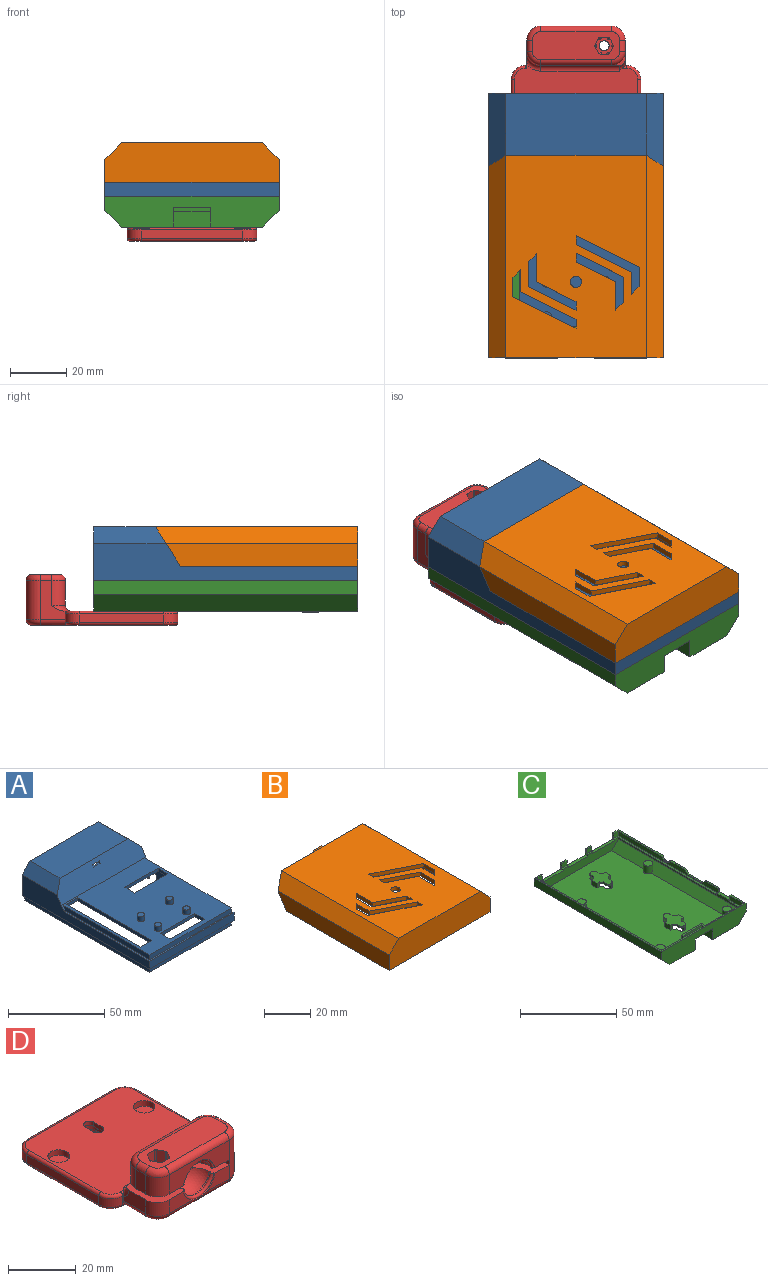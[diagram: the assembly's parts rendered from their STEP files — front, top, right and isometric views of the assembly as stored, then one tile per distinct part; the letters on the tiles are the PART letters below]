
ASSEMBLY  parts=4 mates=1
PART A: 83 faces, bbox 62x94x22 mm
  f0: plane 94x62mm, normal (0,0,-1), area 195.6mm2, adj f3,f4,f11,f16,f26,f27,f28,f43
  f1: plane 64x3mm, normal (-1,0,0), area 189.1mm2, adj f2,f25,f37,f39
  f2: plane 64x60mm, normal (0,0,1), area 2976.4mm2, adj f1,f25,f38,f39,f63,f64,f65,f66
  f3: plane 94x13mm, normal (-1,0,0), area 696.9mm2, adj f0,f4,f24,f25,f26,f37
  f4: plane 62x5mm, normal (0,-1,0), area 310mm2, adj f0,f3,f27,f37
  f5: plane 14.2x2mm, normal (0,0,-1), area 28.4mm2, adj f16,f17,f26,f29
  f6: plane 14.2x2mm, normal (0,0,-1), area 28.4mm2, adj f18,f19,f26,f29
  f7: plane 16.2x2mm, normal (0,0,-1), area 32.4mm2, adj f20,f21,f26,f29
  f8: plane 15.4x2mm, normal (0,0,-1), area 30.8mm2, adj f10,f11,f27,f28
  f9: cylinder r=3.1mm len=6.2mm, axis (1,0,0), area 23.1mm2, adj f14,f15,f27,f28,f54,f57
  f10: plane 7.2x2mm, normal (0,-1,0), area 11.4mm2, adj f8,f14,f27,f28,f58,f59
  f11: plane 7.2x2mm, normal (0,1,0), area 11.4mm2, adj f0,f8,f27,f28,f60,f62
  f12: plane 3.8x1mm, normal (0,0,-1), area 3.8mm2, adj f19,f20,f26,f51
  f13: plane 4x1mm, normal (0,0,-1), area 4mm2, adj f17,f18,f26,f49
  f14: plane 10.63x1mm, normal (0,0,-1), area 10.6mm2, adj f9,f10,f27,f58
  f15: plane 33.03x4.4mm, normal (0,0,-1), area 36.4mm2, adj f9,f21,f26,f27,f53,f55
  f16: plane 14.05x2mm, normal (1,0,0), area 25.1mm2, adj f0,f5,f26,f29,f44,f48
  f17: plane 14.05x2mm, normal (-1,0,0), area 25.1mm2, adj f5,f13,f26,f29,f49,f50
  f18: plane 14.05x2mm, normal (1,0,0), area 25.1mm2, adj f6,f13,f26,f29,f49,f50
  f19: plane 14.05x2mm, normal (-1,0,0), area 25.1mm2, adj f6,f12,f26,f29,f51,f52
  f20: plane 13.05x2mm, normal (1,0,0), area 23.1mm2, adj f7,f12,f26,f29,f51,f52
  f21: plane 13.05x2mm, normal (-1,0,0), area 23.1mm2, adj f7,f15,f26,f29,f55,f56
  f22: plane 25.82x6mm, normal (0.71,0,0.71), area 202.9mm2, adj f23,f25,f26,f27
  f23: plane 50x22mm, normal (0,0,1), area 1100mm2, adj f22,f24,f25,f26
  f24: plane 25.82x6mm, normal (-0.71,0,0.71), area 202.9mm2, adj f3,f23,f25,f26
  f25: plane 62x14mm, normal (0,-0.84,0.54), area 765.6mm2, adj f1,f2,f3,f22,f23,f24,f27,f33
  f26: plane 62x19mm, normal (0,1,0), area 665.4mm2, adj f0,f3,f5,f6,f7,f12,f13,f15
  f27: plane 94x13mm, normal (1,0,0), area 611.6mm2, adj f0,f4,f8,f9,f10,f11,f14,f15
  f28: plane 90x16mm, normal (-1,0,0), area 808.9mm2, adj f0,f8,f9,f10,f11,f29,f30,f31
  f29: plane 58x20mm, normal (0,-1,0), area 533.6mm2, adj f5,f6,f7,f16,f17,f18,f19,f20
  f30: plane 63x58mm, normal (0,0,-1), area 2835.8mm2, adj f28,f31,f35,f36,f63,f64,f65,f66
  f31: plane 58x11mm, normal (0,0.84,-0.54), area 730mm2, adj f28,f30,f32,f33,f34,f36,f40,f41
  f32: plane 22.55x4mm, normal (-0.71,0,-0.71), area 120.3mm2, adj f28,f29,f31,f33
  f33: plane 50x21.27mm, normal (0,0,-1), area 1006.5mm2, adj f25,f29,f31,f32,f34,f40,f41
  f34: plane 22.55x4mm, normal (0.71,0,-0.71), area 120.3mm2, adj f29,f31,f33,f36
  f35: plane 58x9mm, normal (0,1,0), area 522mm2, adj f28,f30,f36,f48
  f36: plane 90x16mm, normal (1,0,0), area 983.4mm2, adj f29,f30,f31,f34,f35,f48
  f37: plane 63.09x62mm, normal (0,0,1), area 186.2mm2, adj f1,f3,f4,f25,f27,f38,f39
  f38: plane 64x3mm, normal (1,0,0), area 189.1mm2, adj f2,f25,f37,f39
  f39: plane 60x3mm, normal (0,-1,0), area 180mm2, adj f1,f2,f37,f38
  f40: plane 2.04x1.2mm, normal (1,0,0), area 1.5mm2, adj f25,f31,f33,f42
  f41: plane 2.04x1.2mm, normal (-1,0,0), area 1.5mm2, adj f25,f31,f33,f42
  f42: plane 5.1x1.27mm, normal (0,0,1), area 6.5mm2, adj f25,f31,f40,f41
  f43: plane 92x3mm, normal (-1,0,0), area 276mm2, adj f0,f44,f47,f48
  f44: plane 4.2x3mm, normal (0,1,0), area 12.6mm2, adj f0,f16,f43,f48
  f45: plane 3x1mm, normal (0,1,0), area 3mm2, adj f0,f28,f46,f48
  f46: plane 10x3mm, normal (1,0,0), area 30mm2, adj f0,f45,f47,f48
  f47: plane 60x3mm, normal (0,-1,0), area 180mm2, adj f0,f43,f46,f48
  f48: plane 92x60mm, normal (0,0,-1), area 163.2mm2, adj f16,f28,f29,f35,f36,f43,f44,f45
  f49: plane 4x3mm, normal (0,1,0), area 12mm2, adj f13,f17,f18,f50
  f50: plane 4x1mm, normal (0,0,-1), area 4mm2, adj f17,f18,f29,f49
  f51: plane 3.8x3mm, normal (0,1,0), area 11.4mm2, adj f12,f19,f20,f52
  f52: plane 3.8x1mm, normal (0,0,-1), area 3.8mm2, adj f19,f20,f29,f51
  f53: plane 32.03x3mm, normal (1,0,0), area 96.1mm2, adj f15,f54,f55,f56
  f54: plane 3x1mm, normal (0,-1,0), area 3mm2, adj f9,f28,f53,f56
  f55: plane 3.4x3mm, normal (0,1,0), area 10.2mm2, adj f15,f21,f53,f56
  f56: plane 32.03x3.4mm, normal (0,0,-1), area 34.4mm2, adj f21,f28,f29,f53,f54,f55
  f57: plane 3x1mm, normal (0,1,0), area 3mm2, adj f9,f28,f58,f59
  f58: plane 10.63x3mm, normal (1,0,0), area 31.9mm2, adj f10,f14,f57,f59
  f59: plane 10.63x1mm, normal (0,0,-1), area 10.6mm2, adj f10,f28,f57,f58
  f60: plane 9.6x3mm, normal (1,0,0), area 28.8mm2, adj f0,f11,f61,f62
  f61: plane 3x1mm, normal (0,-1,0), area 3mm2, adj f0,f28,f60,f62
  f62: plane 9.6x1mm, normal (0,0,-1), area 9.6mm2, adj f11,f28,f60,f61
  f63: plane 7.3x2mm, normal (1,0,0), area 14.6mm2, adj f2,f30,f64,f65
  f64: plane 24.4x2mm, normal (0,-1,0), area 48.8mm2, adj f2,f30,f63,f66
  f65: plane 24.4x2mm, normal (0,1,0), area 48.8mm2, adj f2,f30,f63,f66
  f66: plane 7.3x2mm, normal (-1,0,0), area 14.6mm2, adj f2,f30,f64,f65
  f67: plane 7.2x2mm, normal (1,0,0), area 14.4mm2, adj f2,f30,f68,f69
  f68: plane 25.2x2mm, normal (0,-1,0), area 50.4mm2, adj f2,f30,f67,f70
  f69: plane 25.2x2mm, normal (0,1,0), area 50.4mm2, adj f2,f30,f67,f70
  f70: plane 7.2x2mm, normal (-1,0,0), area 14.4mm2, adj f2,f30,f68,f69
  f71: plane 54.6x2mm, normal (1,0,0), area 109.2mm2, adj f2,f30,f72,f73
  f72: plane 8.4x2mm, normal (0,-1,0), area 16.8mm2, adj f2,f30,f71,f74
  f73: plane 8.4x2mm, normal (0,1,0), area 16.8mm2, adj f2,f30,f71,f74
  f74: plane 54.6x2mm, normal (-1,0,0), area 109.2mm2, adj f2,f30,f72,f73
  f75: cylinder r=1.9mm len=3.8mm, axis (0,0,-1), area 35.8mm2, adj f2,f76
  f76: plane 3.8x3.8mm, normal (0,0,1), area 11.3mm2, adj f75
  f77: cylinder r=1.9mm len=3.8mm, axis (0,0,-1), area 35.8mm2, adj f2,f78
  f78: plane 3.8x3.8mm, normal (0,0,1), area 11.3mm2, adj f77
  f79: cylinder r=1.9mm len=3.8mm, axis (0,0,-1), area 35.8mm2, adj f2,f80
  f80: plane 3.8x3.8mm, normal (0,0,1), area 11.3mm2, adj f79
  f81: cylinder r=1.9mm len=3.8mm, axis (0,0,-1), area 35.8mm2, adj f2,f82
  f82: plane 3.8x3.8mm, normal (0,0,1), area 11.3mm2, adj f81
PART B: 55 faces, bbox 62x74.9x14 mm
  f0: plane 68.18x8mm, normal (1,0,0), area 525.1mm2, adj f4,f6,f7,f54
  f1: plane 68.18x8mm, normal (-1,0,0), area 525.1mm2, adj f4,f6,f8,f54
  f2: plane 68.73x4.83mm, normal (-0.71,0,-0.71), area 446.1mm2, adj f4,f35,f36,f37,f42,f43,f44
  f3: plane 68.73x4.83mm, normal (0.71,0,-0.71), area 446.1mm2, adj f4,f35,f36,f38,f39,f40,f41
  f4: plane 62x14mm, normal (0,0.84,-0.54), area 181.7mm2, adj f0,f1,f2,f3,f5,f7,f8,f9
  f5: plane 72x50mm, normal (0,0,1), area 3265.5mm2, adj f4,f6,f7,f8,f10,f11,f12,f13
  f6: plane 62x14mm, normal (0,-1,0), area 832mm2, adj f0,f1,f5,f7,f8,f54
  f7: plane 72x6mm, normal (0.71,0,0.71), area 594.7mm2, adj f0,f4,f5,f6
  f8: plane 72x6mm, normal (-0.71,0,0.71), area 594.7mm2, adj f1,f4,f5,f6
  f9: plane 64x60mm, normal (0,0,-1), area 186mm2, adj f4,f36,f37,f38,f51,f52,f53
  f10: cylinder r=2mm len=4mm, axis (0,0,1), area 25.1mm2, adj f5,f35
  f11: plane 3.13x2mm, normal (-1,0,0), area 6.3mm2, adj f5,f12,f16,f35
  f12: plane 19.6x9.8mm, normal (-0.45,-0.89,0), area 43.8mm2, adj f5,f11,f13,f35
  f13: plane 7.86x2mm, normal (-1,0,0), area 15.7mm2, adj f5,f12,f14,f35
  f14: plane 2.8x2.8mm, normal (0.71,-0.71,0), area 7.9mm2, adj f5,f13,f15,f35
  f15: plane 6.79x2mm, normal (1,0,0), area 13.6mm2, adj f5,f14,f16,f35
  f16: plane 22.4x11.2mm, normal (0.45,0.89,0), area 50.1mm2, adj f5,f11,f15,f35
  f17: plane 3.13x2mm, normal (1,0,0), area 6.3mm2, adj f5,f18,f22,f35
  f18: plane 14x7mm, normal (0.45,0.89,0), area 31.3mm2, adj f5,f17,f19,f35
  f19: plane 10x2mm, normal (1,0,0), area 20mm2, adj f5,f18,f20,f35
  f20: plane 2.8x2.8mm, normal (-0.71,0.71,0), area 7.9mm2, adj f5,f19,f21,f35
  f21: plane 8.93x2mm, normal (-1,0,0), area 17.9mm2, adj f5,f20,f22,f35
  f22: plane 16.8x8.4mm, normal (-0.45,-0.89,0), area 37.6mm2, adj f5,f17,f21,f35
  f23: plane 3.13x2mm, normal (-1,0,0), area 6.3mm2, adj f5,f24,f28,f35
  f24: plane 14x7mm, normal (-0.45,-0.89,0), area 31.3mm2, adj f5,f23,f25,f35
  f25: plane 10x2mm, normal (-1,0,0), area 20mm2, adj f5,f24,f26,f35
  f26: plane 2.8x2.8mm, normal (0.71,-0.71,0), area 7.9mm2, adj f5,f25,f27,f35
  f27: plane 8.93x2mm, normal (1,0,0), area 17.9mm2, adj f5,f26,f28,f35
  f28: plane 16.8x8.4mm, normal (0.45,0.89,0), area 37.6mm2, adj f5,f23,f27,f35
  f29: plane 3.13x2mm, normal (1,0,0), area 6.3mm2, adj f5,f30,f34,f35
  f30: plane 19.6x9.8mm, normal (0.45,0.89,0), area 43.8mm2, adj f5,f29,f31,f35
  f31: plane 7.86x2mm, normal (1,0,0), area 15.7mm2, adj f5,f30,f32,f35
  f32: plane 2.8x2.8mm, normal (-0.71,0.71,0), area 7.9mm2, adj f5,f31,f33,f35
  f33: plane 6.79x2mm, normal (-1,0,0), area 13.6mm2, adj f5,f32,f34,f35
  f34: plane 22.4x11.2mm, normal (-0.45,-0.89,0), area 50.1mm2, adj f5,f29,f33,f35
  f35: plane 68.73x48.8mm, normal (0,0,-1), area 2984.5mm2, adj f2,f3,f4,f10,f11,f12,f13,f14
  f36: plane 58x9mm, normal (0,1,0), area 498.7mm2, adj f2,f3,f9,f35,f37,f38
  f37: plane 65.65x4.17mm, normal (-1,0,0), area 268.3mm2, adj f2,f4,f9,f36
  f38: plane 65.65x4.17mm, normal (1,0,0), area 268.3mm2, adj f3,f4,f9,f36
  f39: plane 0.23x0.23mm, normal (0,-1,0), area 0mm2, adj f3,f35,f40
  f40: plane 39.26x0.23mm, normal (1,0,0), area 9mm2, adj f3,f35,f39,f41
  f41: plane 0.23x0.23mm, normal (0,1,0), area 0mm2, adj f3,f35,f40
  f42: plane 39.26x0.23mm, normal (-1,0,0), area 9mm2, adj f2,f35,f43,f44
  f43: plane 0.23x0.23mm, normal (0,-1,0), area 0mm2, adj f2,f35,f42
  f44: plane 0.23x0.23mm, normal (0,1,0), area 0mm2, adj f2,f35,f42
  f45: plane 5.1x4.2mm, normal (0,0,1), area 21.4mm2, adj f4,f46,f47,f48
  f46: plane 8.4x1.2mm, normal (-1,0,0), area 10.1mm2, adj f35,f45,f47,f49,f50
  f47: plane 5.1x1.2mm, normal (0,1,0), area 6.1mm2, adj f45,f46,f48,f50
  f48: plane 8.4x1.2mm, normal (1,0,0), area 10.1mm2, adj f35,f45,f47,f49,f50
  f49: plane 5.1x1.2mm, normal (0,-1,0), area 6.1mm2, adj f35,f46,f48,f50
  f50: plane 8.4x5.1mm, normal (0,0,-1), area 42.8mm2, adj f46,f47,f48,f49
  f51: plane 64x3mm, normal (1,0,0), area 189.1mm2, adj f4,f9,f52,f54
  f52: plane 60x3mm, normal (0,1,0), area 180mm2, adj f9,f51,f53,f54
  f53: plane 64x3mm, normal (-1,0,0), area 189.1mm2, adj f4,f9,f52,f54
  f54: plane 63.09x62mm, normal (0,0,-1), area 186.2mm2, adj f0,f1,f4,f6,f51,f52,f53
PART C: 143 faces, bbox 62x94x11.6 mm
  f0: plane 90x48.34mm, normal (0,0,1), area 4043.5mm2, adj f1,f2,f4,f17,f55,f56,f57,f58
  f1: plane 90x4.83mm, normal (0.71,0,0.71), area 582.2mm2, adj f0,f4,f17,f71,f135,f141
  f2: plane 90x4.83mm, normal (-0.71,0,0.71), area 582.2mm2, adj f0,f4,f17,f18,f137,f139
  f3: plane 94x50mm, normal (0,0,-1), area 3255.1mm2, adj f25,f26,f33,f34,f36,f37,f38,f40
  f4: plane 58x6mm, normal (0,1,0), area 252.7mm2, adj f0,f1,f2,f18,f25,f26,f27,f71
  f5: plane 3.95x2mm, normal (-1,0,0), area 4.9mm2, adj f9,f17,f22,f34,f84,f85
  f6: plane 3.95x2mm, normal (-1,0,0), area 4.9mm2, adj f10,f17,f23,f34,f82,f83
  f7: plane 3.95x2mm, normal (-1,0,0), area 4.9mm2, adj f11,f17,f24,f34,f79,f80
  f8: plane 94x62mm, normal (0,0,1), area 169.2mm2, adj f14,f15,f32,f33,f34,f35,f73,f74
  f9: plane 4x1mm, normal (0,0,1), area 4mm2, adj f5,f19,f34,f84
  f10: plane 3.8x1mm, normal (0,0,1), area 3.8mm2, adj f6,f20,f34,f83
  f11: plane 33.03x4.4mm, normal (0,0,1), area 36.4mm2, adj f7,f21,f32,f34,f80,f81
  f12: plane 10.63x1mm, normal (0,0,1), area 10.6mm2, adj f21,f30,f32,f81
  f13: plane 9.6x1mm, normal (0,0,1), area 9.6mm2, adj f16,f28,f32,f81
  f14: plane 3.95x2mm, normal (1,0,0), area 4.9mm2, adj f8,f17,f22,f34,f72,f77
  f15: plane 2.2x1mm, normal (0,1,0), area 2.2mm2, adj f8,f31,f32,f76
  f16: plane 2.2x1mm, normal (0,-1,0), area 2.2mm2, adj f13,f31,f32,f81
  f17: plane 58x6mm, normal (0,-1,0), area 282.3mm2, adj f0,f1,f2,f5,f6,f7,f14,f18
  f18: plane 90x1.97mm, normal (-1,0,0), area 112.2mm2, adj f2,f4,f17,f31,f72,f75,f78,f79
  f19: plane 3.95x2mm, normal (1,0,0), area 4.9mm2, adj f9,f17,f23,f34,f84,f85
  f20: plane 3.95x2mm, normal (1,0,0), area 4.9mm2, adj f10,f17,f24,f34,f82,f83
  f21: cylinder r=3.1mm len=5.93mm, axis (1,0,0), area 7.9mm2, adj f11,f12,f32,f81
  f22: plane 14.2x2mm, normal (0,0,1), area 28.4mm2, adj f5,f14,f17,f34
  f23: plane 14.2x2mm, normal (0,0,1), area 28.4mm2, adj f6,f17,f19,f34
  f24: plane 16.2x2mm, normal (0,0,1), area 32.4mm2, adj f7,f17,f20,f34
  f25: plane 8x7mm, normal (-1,0,0), area 47mm2, adj f3,f4,f27,f33,f38,f129
  f26: plane 8x7mm, normal (1,0,0), area 47mm2, adj f3,f4,f27,f33,f38,f129
  f27: plane 13x2mm, normal (0,0,-1), area 26mm2, adj f4,f25,f26,f33
  f28: plane 2.7x2.2mm, normal (0,0.63,0.78), area 3.5mm2, adj f13,f29,f32,f81
  f29: plane 10x1mm, normal (0,0,1), area 10mm2, adj f28,f30,f32,f81
  f30: plane 2.7x2.2mm, normal (0,-0.63,0.78), area 3.5mm2, adj f12,f29,f32,f81
  f31: plane 8.4x2mm, normal (0,0,1), area 16.8mm2, adj f15,f16,f18,f32,f75,f78
  f32: plane 94x5mm, normal (1,0,0), area 414mm2, adj f8,f11,f12,f13,f15,f16,f21,f28
  f33: plane 62x11mm, normal (0,-1,0), area 555mm2, adj f3,f8,f25,f26,f27,f32,f35,f36
  f34: plane 62x11mm, normal (0,1,0), area 469.8mm2, adj f3,f5,f6,f7,f8,f9,f10,f11
  f35: plane 94x5mm, normal (-1,0,0), area 470mm2, adj f8,f33,f34,f36
  f36: plane 94x6mm, normal (-0.71,0,-0.71), area 797.6mm2, adj f3,f33,f34,f35
  f37: plane 94x6mm, normal (0.71,0,-0.71), area 797.6mm2, adj f3,f32,f33,f34
  f38: plane 13x5.5mm, normal (0,-1,0), area 71.5mm2, adj f3,f25,f26,f129
  f39: cylinder r=1.8mm len=3.6mm, axis (0,0,1), area 6.8mm2, adj f41,f42
  f40: cylinder r=2.85mm len=5.7mm, axis (0,0,1), area 10.7mm2, adj f3,f41
  f41: plane 5.7x5.7mm, normal (0,0,-1), area 15.3mm2, adj f39,f40
  f42: plane 3.6x3.6mm, normal (0,0,-1), area 10.2mm2, adj f39
  f43: cylinder r=1.8mm len=3.6mm, axis (0,0,1), area 6.8mm2, adj f45,f46
  f44: cylinder r=2.85mm len=5.7mm, axis (0,0,1), area 10.7mm2, adj f3,f45
  f45: plane 5.7x5.7mm, normal (0,0,-1), area 15.3mm2, adj f43,f44
  f46: plane 3.6x3.6mm, normal (0,0,-1), area 10.2mm2, adj f43
  f47: cylinder r=1.8mm len=3.6mm, axis (0,0,1), area 6.8mm2, adj f49,f50
  f48: cylinder r=2.85mm len=5.7mm, axis (0,0,1), area 10.7mm2, adj f3,f49
  f49: plane 5.7x5.7mm, normal (0,0,-1), area 15.3mm2, adj f47,f48
  f50: plane 3.6x3.6mm, normal (0,0,-1), area 10.2mm2, adj f47
  f51: cylinder r=1.8mm len=3.6mm, axis (0,0,1), area 6.8mm2, adj f53,f54
  f52: cylinder r=2.85mm len=5.7mm, axis (0,0,1), area 10.7mm2, adj f3,f53
  f53: plane 5.7x5.7mm, normal (0,0,-1), area 15.3mm2, adj f51,f52
  f54: plane 3.6x3.6mm, normal (0,0,-1), area 10.2mm2, adj f51
  f55: cylinder r=2mm len=4mm, axis (0,0,-1), area 12.6mm2, adj f0,f3,f56,f62
  f56: plane 2x1.94mm, normal (-1,0,0), area 3.9mm2, adj f0,f3,f55,f57
  f57: cylinder r=4mm len=6.93mm, axis (0,0,-1), area 25.1mm2, adj f0,f3,f56,f58,f86,f88,f100
  f58: plane 2x1.94mm, normal (-1,0,0), area 3.9mm2, adj f0,f3,f57,f59
  f59: cylinder r=2mm len=4mm, axis (0,0,-1), area 12.6mm2, adj f0,f3,f58,f60
  f60: plane 2x1.94mm, normal (1,0,0), area 3.9mm2, adj f0,f3,f59,f61
  f61: cylinder r=4mm len=6.93mm, axis (0,0,-1), area 25.1mm2, adj f0,f3,f60,f62,f100,f101,f103
  f62: plane 2x1.94mm, normal (1,0,0), area 3.9mm2, adj f0,f3,f55,f61
  f63: cylinder r=2mm len=4mm, axis (0,0,-1), area 12.6mm2, adj f0,f3,f64,f70
  f64: plane 2x1.94mm, normal (-1,0,0), area 3.9mm2, adj f0,f3,f63,f65
  f65: cylinder r=4mm len=6.93mm, axis (0,0,-1), area 25.1mm2, adj f0,f3,f64,f66,f104,f107,f121
  f66: plane 2x1.94mm, normal (-1,0,0), area 3.9mm2, adj f0,f3,f65,f67
  f67: cylinder r=2mm len=4mm, axis (0,0,-1), area 12.6mm2, adj f0,f3,f66,f68
  f68: plane 2x1.94mm, normal (1,0,0), area 3.9mm2, adj f0,f3,f67,f69
  f69: cylinder r=4mm len=6.93mm, axis (0,0,-1), area 25.1mm2, adj f0,f3,f68,f70,f109,f111,f121
  f70: plane 2x1.94mm, normal (1,0,0), area 3.9mm2, adj f0,f3,f63,f69
  f71: plane 90x1.17mm, normal (1,0,0), area 105.4mm2, adj f1,f4,f17,f72
  f72: plane 92x60mm, normal (0,0,1), area 163.2mm2, adj f4,f14,f17,f18,f71,f73,f74,f75
  f73: plane 60x3mm, normal (0,1,0), area 180mm2, adj f8,f72,f74,f76
  f74: plane 92x3mm, normal (1,0,0), area 276mm2, adj f8,f72,f73,f77
  f75: plane 1x0.8mm, normal (0,-1,0), area 0.8mm2, adj f18,f31,f72,f76
  f76: plane 10x3mm, normal (-1,0,0), area 30mm2, adj f8,f15,f72,f73,f75
  f77: plane 4.2x3mm, normal (0,-1,0), area 12.6mm2, adj f8,f14,f72,f74
  f78: plane 1x0.8mm, normal (0,1,0), area 0.8mm2, adj f18,f31,f79,f81
  f79: plane 73.6x3.4mm, normal (0,0,1), area 76mm2, adj f7,f17,f18,f78,f80,f81
  f80: plane 3.4x3mm, normal (0,-1,0), area 10.2mm2, adj f7,f11,f79,f81
  f81: plane 73.6x3mm, normal (-1,0,0), area 183.3mm2, adj f11,f12,f13,f16,f21,f28,f29,f30
  f82: plane 3.8x1mm, normal (0,0,1), area 3.8mm2, adj f6,f17,f20,f83
  f83: plane 3.8x3mm, normal (0,-1,0), area 11.4mm2, adj f6,f10,f20,f82
  f84: plane 4x3mm, normal (0,-1,0), area 12mm2, adj f5,f9,f19,f85
  f85: plane 4x1mm, normal (0,0,1), area 4mm2, adj f5,f17,f19,f84
  f86: plane 3x1.54mm, normal (0,-1,0), area 4.6mm2, adj f0,f57,f87,f89,f94
  f87: plane 4x3mm, normal (1,0,0), area 12mm2, adj f0,f86,f88,f89
  f88: plane 3x1.54mm, normal (0,1,0), area 4.6mm2, adj f0,f57,f87,f89,f90
  f89: plane 14.8x10mm, normal (0,0,1), area 84.8mm2, adj f86,f87,f88,f90,f91,f92,f93,f94
  f90: cylinder r=4mm len=1.46mm, axis (0,0,-1), area 2.1mm2, adj f88,f89,f93,f100
  f91: cylinder r=4mm len=1.46mm, axis (0,0,-1), area 2.1mm2, adj f89,f99,f100,f101
  f92: cylinder r=2mm len=4mm, axis (0,0,-1), area 6.3mm2, adj f89,f93,f99,f100
  f93: plane 1.94x1mm, normal (1,0,0), area 1.9mm2, adj f89,f90,f92,f100
  f94: cylinder r=4mm len=1.46mm, axis (0,0,-1), area 2.1mm2, adj f86,f89,f95,f100
  f95: plane 1.94x1mm, normal (1,0,0), area 1.9mm2, adj f89,f94,f96,f100
  f96: cylinder r=2mm len=4mm, axis (0,0,-1), area 6.3mm2, adj f89,f95,f97,f100
  f97: plane 1.94x1mm, normal (-1,0,0), area 1.9mm2, adj f89,f96,f98,f100
  f98: cylinder r=4mm len=1.46mm, axis (0,0,-1), area 2.1mm2, adj f89,f97,f100,f103
  f99: plane 1.94x1mm, normal (-1,0,0), area 1.9mm2, adj f89,f91,f92,f100
  f100: plane 14.8x8mm, normal (0,0,-1), area 72.3mm2, adj f57,f61,f90,f91,f92,f93,f94,f95
  f101: plane 3x1.54mm, normal (0,1,0), area 4.6mm2, adj f0,f61,f89,f91,f102
  f102: plane 4x3mm, normal (-1,0,0), area 12mm2, adj f0,f89,f101,f103
  f103: plane 3x1.54mm, normal (0,-1,0), area 4.6mm2, adj f0,f61,f89,f98,f102
  f104: plane 3x1.54mm, normal (0,1,0), area 4.6mm2, adj f0,f65,f105,f106,f108
  f105: plane 14.8x10mm, normal (0,0,1), area 84.8mm2, adj f104,f106,f107,f108,f109,f110,f111,f112
  f106: plane 4x3mm, normal (1,0,0), area 12mm2, adj f0,f104,f105,f107
  f107: plane 3x1.54mm, normal (0,-1,0), area 4.6mm2, adj f0,f65,f105,f106,f115
  f108: cylinder r=4mm len=1.46mm, axis (0,0,-1), area 2.1mm2, adj f104,f105,f114,f121
  f109: plane 3x1.54mm, normal (0,1,0), area 4.6mm2, adj f0,f69,f105,f110,f119
  f110: plane 4x3mm, normal (-1,0,0), area 12mm2, adj f0,f105,f109,f111
  f111: plane 3x1.54mm, normal (0,-1,0), area 4.6mm2, adj f0,f69,f105,f110,f112
  f112: cylinder r=4mm len=1.46mm, axis (0,0,-1), area 2.1mm2, adj f105,f111,f118,f121
  f113: cylinder r=2mm len=4mm, axis (0,0,-1), area 6.3mm2, adj f105,f114,f120,f121
  f114: plane 1.94x1mm, normal (1,0,0), area 1.9mm2, adj f105,f108,f113,f121
  f115: cylinder r=4mm len=1.46mm, axis (0,0,-1), area 2.1mm2, adj f105,f107,f116,f121
  f116: plane 1.94x1mm, normal (1,0,0), area 1.9mm2, adj f105,f115,f117,f121
  f117: cylinder r=2mm len=4mm, axis (0,0,-1), area 6.3mm2, adj f105,f116,f118,f121
  f118: plane 1.94x1mm, normal (-1,0,0), area 1.9mm2, adj f105,f112,f117,f121
  f119: cylinder r=4mm len=1.46mm, axis (0,0,-1), area 2.1mm2, adj f105,f109,f120,f121
  f120: plane 1.94x1mm, normal (-1,0,0), area 1.9mm2, adj f105,f113,f119,f121
  f121: plane 14.8x8mm, normal (0,0,-1), area 72.3mm2, adj f65,f69,f108,f112,f113,f114,f115,f116
  f122: cylinder r=1mm len=2mm, axis (0,0,-1), area 1.3mm2, adj f121,f123
  f123: plane 2x2mm, normal (0,0,-1), area 3.1mm2, adj f122
  f124: cylinder r=1mm len=2mm, axis (0,0,-1), area 1.3mm2, adj f100,f125
  f125: plane 2x2mm, normal (0,0,-1), area 3.1mm2, adj f124
  f126: plane 7x3.5mm, normal (-1,0,0), area 24.5mm2, adj f0,f4,f128,f129
  f127: plane 7x3.5mm, normal (1,0,0), area 24.5mm2, adj f0,f4,f128,f129
  f128: plane 15x3.5mm, normal (0,1,0), area 52.5mm2, adj f0,f126,f127,f129
  f129: plane 15x7mm, normal (0,0,1), area 27mm2, adj f4,f25,f26,f38,f126,f127,f128
  f130: plane 32x0.5mm, normal (-1,0,0), area 16mm2, adj f3,f131,f133,f134
  f131: plane 34x0.5mm, normal (0,1,0), area 17mm2, adj f3,f130,f132,f134
  f132: plane 32x0.5mm, normal (1,0,0), area 16mm2, adj f3,f131,f133,f134
  f133: plane 34x0.5mm, normal (0,-1,0), area 17mm2, adj f3,f130,f132,f134
  f134: plane 34x32mm, normal (0,0,-1), area 1088mm2, adj f130,f131,f132,f133
  f135: cylinder r=2.5mm len=5mm, axis (0,0,-1), area 63.4mm2, adj f0,f1,f136
  f136: plane 5x5mm, normal (0,0,1), area 19.6mm2, adj f135
  f137: cylinder r=2.5mm len=5mm, axis (0,0,-1), area 63.4mm2, adj f0,f2,f138
  f138: plane 5x5mm, normal (0,0,1), area 19.6mm2, adj f137
  f139: cylinder r=2.5mm len=5mm, axis (0,0,-1), area 63.4mm2, adj f0,f2,f140
  f140: plane 5x5mm, normal (0,0,1), area 19.6mm2, adj f139
  f141: cylinder r=2.5mm len=5mm, axis (0,0,-1), area 63.4mm2, adj f0,f1,f142
  f142: plane 5x5mm, normal (0,0,1), area 19.6mm2, adj f141
PART D: 122 faces, bbox 47.4x55.4x18.6 mm
  f0: plane 9.75x5mm, normal (0,-1,0), area 36mm2, adj f33,f34,f81,f93
  f1: plane 9.75x5mm, normal (0,-1,0), area 36mm2, adj f33,f34,f82,f93
  f2: plane 25x7mm, normal (0,1,0), area 175mm2, adj f37,f76,f80,f90
  f3: plane 3.01x0.78mm, normal (0,-1,0), area 1.6mm2, adj f32,f78,f95,f98,f99,f108
  f4: plane 51x44mm, normal (0,0,-1), area 1914.7mm2, adj f91,f92,f93,f94,f95,f108,f109,f110
  f5: cylinder r=1.8mm len=3.6mm, axis (0,0,1), area 8.5mm2, adj f6,f8,f12,f21
  f6: plane 3.4x1.5mm, normal (1,0,0), area 5.1mm2, adj f5,f7,f12,f21
  f7: cylinder r=1.8mm len=3.6mm, axis (0,0,1), area 8.5mm2, adj f6,f8,f12,f21
  f8: plane 3.4x1.5mm, normal (-1,0,0), area 5.1mm2, adj f5,f7,f12,f21
  f9: plane 30x3mm, normal (1,0,0), area 90mm2, adj f23,f77,f105,f114
  f10: plane 30x3mm, normal (-1,0,0), area 90mm2, adj f22,f78,f101,f110
  f11: plane 36x3mm, normal (0,1,0), area 108mm2, adj f22,f23,f103,f112
  f12: plane 44.04x39.14mm, normal (0,0,1), area 1541.3mm2, adj f5,f6,f7,f8,f13,f15,f38,f96
  f13: cylinder r=3.2mm len=6.4mm, axis (0,0,1), area 40.2mm2, adj f12,f14
  f14: plane 6.4x6.4mm, normal (0,0,1), area 32.2mm2, adj f13
  f15: cylinder r=3.2mm len=6.4mm, axis (0,0,1), area 40.2mm2, adj f12,f16
  f16: plane 6.4x6.4mm, normal (0,0,1), area 32.2mm2, adj f15
  f17: plane 3.4x2.5mm, normal (1,0,0), area 8.5mm2, adj f18,f20,f21,f118
  f18: cylinder r=3.3mm len=6.6mm, axis (0,0,-1), area 25.9mm2, adj f17,f19,f21,f120
  f19: plane 3.4x2.5mm, normal (-1,0,0), area 8.5mm2, adj f18,f20,f21,f121
  f20: cylinder r=3.3mm len=6.6mm, axis (0,0,-1), area 25.9mm2, adj f17,f19,f21,f119
  f21: plane 10x6.6mm, normal (0,0,-1), area 34.2mm2, adj f5,f6,f7,f8,f17,f18,f19,f20
  f22: cylinder r=5mm len=5mm, axis (0,0,-1), area 23.6mm2, adj f10,f11,f102,f111
  f23: cylinder r=5mm len=5mm, axis (0,0,1), area 23.6mm2, adj f9,f11,f104,f113
  f24: plane 3x0.77mm, normal (0,-1,0), area 1.6mm2, adj f38,f77,f91,f107,f115
  f25: cylinder r=1.75mm len=3.5mm, axis (0,0,-1), area 38.5mm2, adj f34,f74
  f26: sphere r=6.1mm, area 97.7mm2, adj f27,f34
  f27: cone r=6.1mm half-angle=14.7deg, axis (0,-1,0), area 7.5mm2, adj f26,f28,f34
  f28: torus R=6.36mm, axis (0,-1,0), area 31.7mm2, adj f27,f33,f34
  f29: sphere r=6.1mm, area 97.7mm2, adj f30,f37
  f30: cone r=6.1mm half-angle=14.7deg, axis (0,-1,0), area 7.5mm2, adj f29,f31,f37
  f31: torus R=6.36mm, axis (0,-1,0), area 31.7mm2, adj f30,f36,f37
  f32: plane 9x5mm, normal (-1,0,0), area 40.1mm2, adj f3,f34,f81,f95,f98
  f33: cone r=6.52mm half-angle=14.7deg, axis (0,-1,0), area 6.1mm2, adj f0,f1,f28,f34,f93
  f34: plane 30x14mm, normal (0,0,1), area 324.6mm2, adj f0,f1,f25,f26,f27,f28,f32,f33
  f35: plane 14x2mm, normal (-1,0,0), area 28mm2, adj f34,f37,f76,f82
  f36: cone r=6.52mm half-angle=14.7deg, axis (0,-1,0), area 6.1mm2, adj f31,f37,f39
  f37: plane 30x14mm, normal (0,0,-1), area 320.1mm2, adj f2,f29,f30,f31,f35,f36,f39,f40
  f38: plane 14.58x10.58mm, normal (1,0,0), area 74.8mm2, adj f12,f24,f76,f82,f87,f91,f97,f107
  f39: plane 25x7mm, normal (0,-1,0), area 119.7mm2, adj f36,f37,f79,f82,f83
  f40: plane 7x4mm, normal (-1,0,0), area 28mm2, adj f37,f79,f80,f86
  f41: plane 31x10mm, normal (0,0,1), area 271.5mm2, adj f62,f63,f64,f65,f66,f67,f68,f69
  f42: cone r=0.25mm half-angle=45deg, axis (0,0,1), area 0.7mm2, adj f43,f55,f72,f73
  f43: cylinder r=0.75mm len=2mm, axis (0,0,1), area 3.1mm2, adj f42,f59,f72,f73
  f44: cone r=0.25mm half-angle=45deg, axis (0,0,1), area 0.7mm2, adj f45,f55,f71,f72
  f45: cylinder r=0.75mm len=2mm, axis (0,0,1), area 3.1mm2, adj f44,f60,f71,f72
  f46: cone r=0.25mm half-angle=45deg, axis (0,0,1), area 0.7mm2, adj f47,f55,f70,f71
  f47: cylinder r=0.75mm len=2mm, axis (0,0,1), area 3.1mm2, adj f46,f61,f70,f71
  f48: cone r=0.25mm half-angle=45deg, axis (0,0,1), area 0.7mm2, adj f49,f55,f69,f70
  f49: cylinder r=0.75mm len=2mm, axis (0,0,1), area 3.1mm2, adj f48,f56,f69,f70
  f50: cone r=0.25mm half-angle=45deg, axis (0,0,1), area 0.7mm2, adj f51,f55,f68,f69
  f51: cylinder r=0.75mm len=2mm, axis (0,0,1), area 3.1mm2, adj f50,f57,f68,f69
  f52: cylinder r=0.75mm len=2mm, axis (0,0,1), area 3.1mm2, adj f53,f58,f68,f73
  f53: cone r=0.25mm half-angle=45deg, axis (0,0,1), area 0.7mm2, adj f52,f55,f68,f73
  f54: cylinder r=1.75mm len=3.5mm, axis (0,0,-1), area 22mm2, adj f37,f55
  f55: plane 6.68x6mm, normal (0,0,1), area 21.2mm2, adj f42,f44,f46,f48,f50,f53,f54,f68
  f56: cone r=0.75mm half-angle=45deg, axis (0,0,-1), area 0.7mm2, adj f49,f65,f69,f70
  f57: cone r=0.75mm half-angle=45deg, axis (0,0,-1), area 0.7mm2, adj f51,f66,f68,f69
  f58: cone r=0.75mm half-angle=45deg, axis (0,0,-1), area 0.7mm2, adj f52,f67,f68,f73
  f59: cone r=0.75mm half-angle=45deg, axis (0,0,-1), area 0.7mm2, adj f43,f62,f72,f73
  f60: cone r=0.75mm half-angle=45deg, axis (0,0,-1), area 0.7mm2, adj f45,f63,f71,f72
  f61: cone r=0.75mm half-angle=45deg, axis (0,0,-1), area 0.7mm2, adj f47,f64,f70,f71
  f62: cylinder r=0.25mm len=4mm, axis (0,0,-1), area 2.1mm2, adj f41,f59,f72,f73
  f63: cylinder r=0.25mm len=4mm, axis (0,0,-1), area 2.1mm2, adj f41,f60,f71,f72
  f64: cylinder r=0.25mm len=4mm, axis (0,0,-1), area 2.1mm2, adj f41,f61,f70,f71
  f65: cylinder r=0.25mm len=4mm, axis (0,0,-1), area 2.1mm2, adj f41,f56,f69,f70
  f66: cylinder r=0.25mm len=4mm, axis (0,0,-1), area 2.1mm2, adj f41,f57,f68,f69
  f67: cylinder r=0.25mm len=4mm, axis (0,0,-1), area 2.1mm2, adj f41,f58,f68,f73
  f68: plane 7x2.57mm, normal (0.87,0.5,0), area 18.2mm2, adj f41,f50,f51,f52,f53,f55,f57,f58
  f69: plane 7x2.57mm, normal (0.87,-0.5,0), area 18.2mm2, adj f41,f48,f49,f50,f51,f55,f56,f57
  f70: plane 7x2.96mm, normal (0,-1,0), area 18.2mm2, adj f41,f46,f47,f48,f49,f55,f56,f61
  f71: plane 7x2.57mm, normal (-0.87,-0.5,0), area 18.2mm2, adj f41,f44,f45,f46,f47,f55,f60,f61
  f72: plane 7x2.57mm, normal (-0.87,0.5,0), area 18.2mm2, adj f41,f42,f43,f44,f45,f55,f59,f60
  f73: plane 7x2.96mm, normal (0,1,0), area 18.2mm2, adj f41,f42,f43,f52,f53,f55,f58,f59
  f74: plane 6.4x6.4mm, normal (0,0,-1), area 22.5mm2, adj f25,f75
  f75: cylinder r=3.2mm len=6.4mm, axis (0,0,-1), area 50.3mm2, adj f74,f117
  f76: cylinder r=5mm len=9mm, axis (0,0,-1), area 70.7mm2, adj f2,f35,f38,f89,f97
  f77: cylinder r=5mm len=5mm, axis (0,0,-1), area 23.6mm2, adj f9,f24,f106,f116
  f78: cylinder r=5mm len=5mm, axis (0,0,1), area 23.6mm2, adj f3,f10,f100,f109
  f79: cylinder r=5mm len=7mm, axis (0,0,-1), area 55mm2, adj f37,f39,f40,f84
  f80: cylinder r=5mm len=7mm, axis (0,0,1), area 55mm2, adj f2,f37,f40,f88
  f81: cylinder r=5mm len=5mm, axis (0,0,-1), area 39.3mm2, adj f0,f32,f34,f94
  f82: cylinder r=5mm len=14mm, axis (0,0,1), area 110mm2, adj f1,f35,f38,f39,f85,f92
  f83: cylinder r=2mm len=25mm, axis (-1,0,0), area 78.5mm2, adj f39,f41,f84,f85
  f84: torus R=3mm, axis (0,0,-1), area 21.1mm2, adj f41,f79,f83,f86
  f85: torus R=3mm, axis (0,0,-1), area 21.1mm2, adj f41,f82,f83,f87
  f86: cylinder r=2mm len=4mm, axis (0,1,0), area 12.6mm2, adj f40,f41,f84,f88
  f87: cylinder r=2mm len=4mm, axis (0,-1,0), area 12.6mm2, adj f38,f41,f85,f89
  f88: torus R=3mm, axis (0,0,-1), area 21.1mm2, adj f41,f80,f86,f90
  f89: torus R=3mm, axis (0,0,-1), area 21.1mm2, adj f41,f76,f87,f90
  f90: cylinder r=2mm len=25mm, axis (1,0,0), area 78.5mm2, adj f2,f41,f88,f89
  f91: cylinder r=2mm len=10mm, axis (0,1,0), area 29.3mm2, adj f4,f24,f38,f92,f115
  f92: torus R=3mm, axis (0,0,-1), area 21.1mm2, adj f4,f82,f91,f93
  f93: cylinder r=2mm len=25mm, axis (-1,0,0), area 76.4mm2, adj f0,f1,f4,f33,f92,f94
  f94: torus R=3mm, axis (0,0,-1), area 21.1mm2, adj f4,f81,f93,f95
  f95: cylinder r=2mm len=10mm, axis (0,-1,0), area 29.3mm2, adj f3,f4,f32,f94,f108
  f96: cylinder r=2mm len=28mm, axis (-1,0,0), area 88mm2, adj f12,f34,f97,f98
  f97: torus R=7mm, axis (0,0,-1), area 20.9mm2, adj f12,f38,f76,f96
  f98: torus R=4mm, axis (1,0,0), area 9.1mm2, adj f3,f12,f32,f34,f96,f99
  f99: cylinder r=1mm len=1.56mm, axis (-1,0,0), area 1.6mm2, adj f3,f12,f98,f100
  f100: torus R=4mm, axis (0,0,-1), area 11.4mm2, adj f12,f78,f99,f101
  f101: cylinder r=1mm len=30mm, axis (0,1,0), area 47.1mm2, adj f10,f12,f100,f102
  f102: torus R=4mm, axis (0,0,-1), area 11.4mm2, adj f12,f22,f101,f103
  f103: cylinder r=1mm len=36mm, axis (1,0,0), area 56.5mm2, adj f11,f12,f102,f104
  f104: torus R=4mm, axis (0,0,-1), area 11.4mm2, adj f12,f23,f103,f105
  f105: cylinder r=1mm len=30mm, axis (0,-1,0), area 47.1mm2, adj f9,f12,f104,f106
  f106: torus R=4mm, axis (0,0,-1), area 11.4mm2, adj f12,f77,f105,f107
  f107: cylinder r=1mm len=1mm, axis (-1,0,0), area 0.8mm2, adj f12,f24,f38,f106
  f108: cylinder r=1mm len=2.5mm, axis (1,0,0), area 2.6mm2, adj f3,f4,f95,f109
  f109: torus R=4mm, axis (0,0,-1), area 11.4mm2, adj f4,f78,f108,f110
  f110: cylinder r=1mm len=30mm, axis (0,-1,0), area 47.1mm2, adj f4,f10,f109,f111
  f111: torus R=4mm, axis (0,0,-1), area 11.4mm2, adj f4,f22,f110,f112
  f112: cylinder r=1mm len=36mm, axis (-1,0,0), area 56.5mm2, adj f4,f11,f111,f113
  f113: torus R=4mm, axis (0,0,-1), area 11.4mm2, adj f4,f23,f112,f114
  f114: cylinder r=1mm len=30mm, axis (0,1,0), area 47.1mm2, adj f4,f9,f113,f116
  f115: cylinder r=1mm len=2.5mm, axis (1,0,0), area 2.6mm2, adj f4,f24,f91,f116
  f116: torus R=4mm, axis (0,0,-1), area 11.4mm2, adj f4,f77,f114,f115
  f117: torus R=4.2mm, axis (0,0,-1), area 35.2mm2, adj f4,f75
  f118: cylinder r=1mm len=3.4mm, axis (0,-1,0), area 5.3mm2, adj f4,f17,f119,f120
  f119: torus R=4.3mm, axis (0,0,-1), area 18.1mm2, adj f4,f20,f118,f121
  f120: torus R=4.3mm, axis (0,0,-1), area 18.1mm2, adj f4,f18,f118,f121
  f121: cylinder r=1mm len=3.4mm, axis (0,1,0), area 5.3mm2, adj f4,f19,f119,f120
PLACE A at identity
PLACE B at identity
PLACE C at identity fixed
PLACE D rot(axis=(0,0,1),180deg) t=(52.05,-133.72,-8.15)mm
MATE fastened C.f39 <-> D.f13  axis (0,0,-1) through (17.85,-16.85,-15)mm
